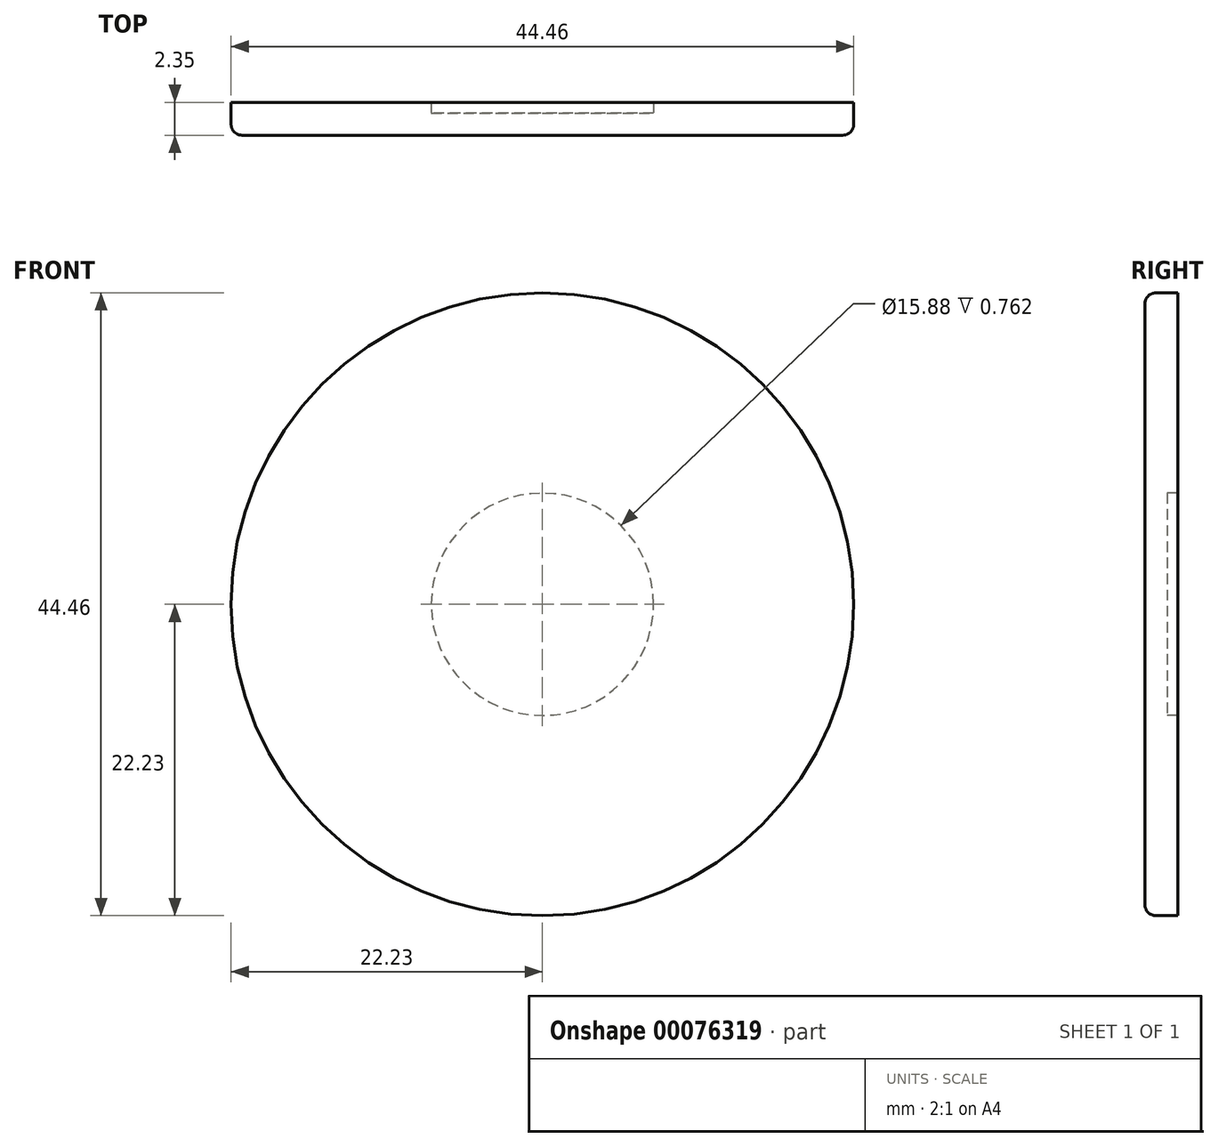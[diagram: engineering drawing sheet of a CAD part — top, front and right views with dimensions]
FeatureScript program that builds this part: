
annotation { "Feature Type Name" : "Feature", "Feature Type Description" : "" }
export const myFeature = defineFeature(function(context is Context, id is Id, definition is map)
    precondition{}
    {
        {
            var Q0;
            Q0=qCreatedBy(makeId("Front.planeOp"),FACE);
            var sketch = newSketch(context, id + "F0", { "sketchPlane" : qUnion([Q0])});
            skCircle(sketch, "E0", {"center": v(0, 0) * mm, "radius": 22.23 * mm});
            skSolve(sketch);
        }
        {
            var Q0;
            Q0=makeQuery(id+"F0.imprint","IMPRINT",FACE,{"disambiguationData":[TD([[makeQuery(id+"F0.imprint","IMPRINT",EDGE,{"derivedFrom":sQuery(id+"F0.wireOp",EDGE,"E0")}),1.0]])]});
            extrude(context, id + "F1", {"entities" : qUnion([Q0]), "depth" : 1.59 * mm});
        }
        {
            var Q0;
            Q0=makeQuery(id+"F1.opExtrude","CAP_EDGE",EDGE,{"disambiguationData":[OSD([sQuery(id+"F0.wireOp",EDGE,"E0")])],"isStart":false});
            fillet(context, id + "F2", {"entities" : qUnion([Q0]), "radius" : 0.8 * mm, "tangentPropagation" : true, "allowEdgeOverflow" : false});
        }
        {
            var Q0;
            Q0=makeQuery(id+"F1.opExtrude","CAP_FACE",FACE,{"disambiguationData":[OSD([sQuery(id+"F0.wireOp",EDGE,"E0")])],"isStart":true});
            var sketch = newSketch(context, id + "F3", { "sketchPlane" : qUnion([Q0])});
            skCircle(sketch, "E1", {"center": v(0, 0) * mm, "radius": 7.94 * mm});
            skSolve(sketch);
        }
        {
            var Q0;
            Q0=makeQuery(id+"F3.imprint","IMPRINT",FACE,{"disambiguationData":[TD([[makeQuery(id+"F3.imprint","IMPRINT",EDGE,{"derivedFrom":sQuery(id+"F3.wireOp",EDGE,"E1")}),-1.0]])]});
            extrude(context, id + "F4", {"entities" : qUnion([Q0]), "operationType" : NewBodyOperationType.ADD, "depth" : 0.76 * mm});
        }
    });
